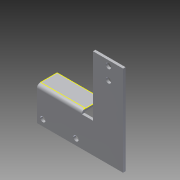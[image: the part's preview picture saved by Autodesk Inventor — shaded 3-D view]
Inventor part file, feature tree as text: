
AUTODESK INVENTOR PART (.ipt)
format: ipt  version: 2013 (Build 170138000, 138)  size: 175,616 bytes
history: native  units: in
note: dims shown in document units (in); Inventor stores cm internally (conversion verified against a paired STEP export)
features: sketch x8, other x6, sheet_metal_op x4, reference x4, extrude x2
ambient origin geometry x8: Origin, YZ Plane, XZ Plane, XY Plane, X Axis, Y Axis, Z Axis, Center Point
bodies: Solid1 (feature_tree)
feature tree (24):
  sheet_metal_op  "Face1"
  sheet_metal_op  "Flange1"
  sketch  "Sketch9"  dims[d8=0.125in]
  extrude  "Extrusion1"  Depth=1.5in
  extrude  "Extrusion2"  Depth=1.181in
  sketch  "Sketch1"  dims[d1=2.244in d2=1.5in]
  other  "Plate1"
  sketch  "Sketch2"  dims[d3=0.295in d4=1.181in]
  other  "Plate2"
  sheet_metal_op  "Bend1"
  sheet_metal_op  "Corner1"
  sketch  "Sketch8"  dims[d5=0.295in]
  reference  "Reference1"
  reference  "Reference2"
  sketch  "Sketch10"  dims[d9=0.125in]
  sketch  "Sketch13"  dims[d10=0.0625in]
  sketch  "Sketch14"  dims[d11=0.25in]
  reference  "Reference7"
  reference  "Reference8"
  sketch  "Sketch15"  dims[d12=0.125in d13=1.0in d14=90.0deg d15=0.05in d16=0.5in d17=0.125in d18=0.125in d19=0.125in d20=0.0in d21=2.053in d22=0.0in d27=3.0in d28=0.0in d29=0.125in d30=0.0in d31=1.5in d32=0.125in d33=0.0in]
  other  "Cut1"
  other  "Cut4"
  other  "Cut5"
  other  "Definition1"
